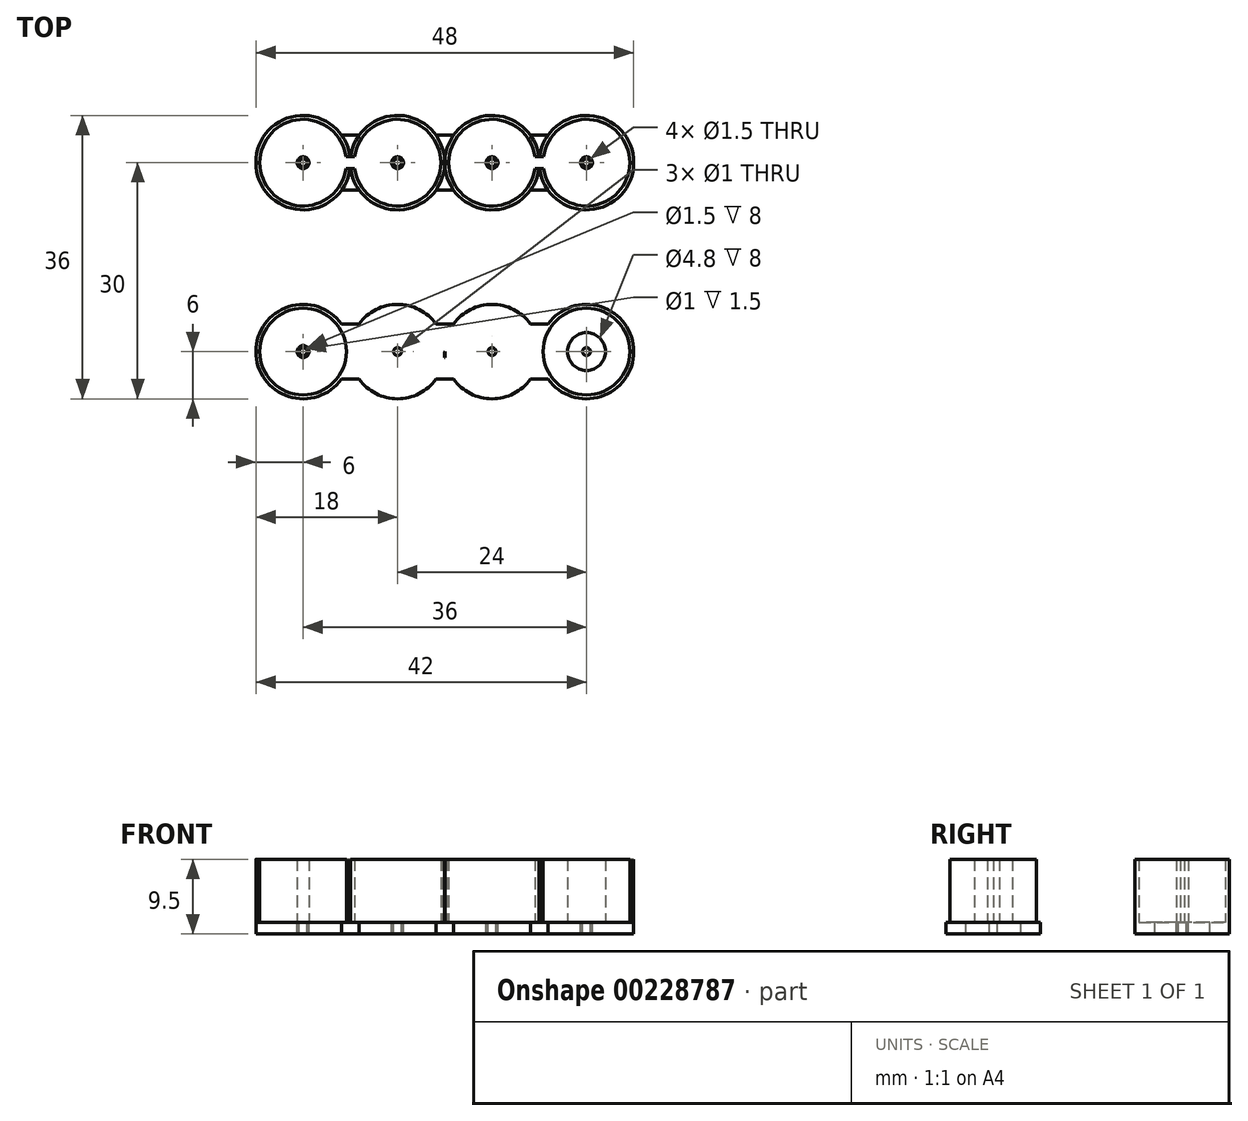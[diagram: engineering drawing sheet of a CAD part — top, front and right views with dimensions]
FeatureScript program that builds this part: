
annotation { "Feature Type Name" : "Feature", "Feature Type Description" : "" }
export const myFeature = defineFeature(function(context is Context, id is Id, definition is map)
    precondition{}
    {
        {
            var Q0;
            Q0=qCreatedBy(makeId("Top.planeOp"),FACE);
            var sketch = newSketch(context, id + "F0", { "sketchPlane" : qUnion([Q0])});
            skCircle(sketch, "E0", {"center": v(-18, 0) * mm, "radius": 6 * mm});
            skCircle(sketch, "E1", {"center": v(-6, 0) * mm, "radius": 6 * mm});
            skCircle(sketch, "E2", {"center": v(6, 0) * mm, "radius": 6 * mm});
            skCircle(sketch, "E3", {"center": v(18, 0) * mm, "radius": 6 * mm});
            skPoint(sketch, "E4", {"position": v(0, 0) * mm});
            skCircle(sketch, "E5", {"center": v(-18, 0) * mm, "radius": 5.5 * mm});
            skCircle(sketch, "E6", {"center": v(-6, 0) * mm, "radius": 5.5 * mm});
            skCircle(sketch, "E7", {"center": v(6, 0) * mm, "radius": 5.5 * mm});
            skCircle(sketch, "E8", {"center": v(18, 0) * mm, "radius": 5.5 * mm});
            skLineSegment(sketch, "E9", {"start": v(0, 0) * mm, "end": v(0, -12) * mm, "construction": true});
            skLineSegment(sketch, "E10", {"start": v(0, -12) * mm, "end": v(-21.8, -12) * mm, "construction": true});
            skCircle(sketch, "E11.MirrorC", {"center": v(-18, -24) * mm, "radius": 6 * mm});
            skCircle(sketch, "E12.MirrorC", {"center": v(-6, -24) * mm, "radius": 6 * mm});
            skCircle(sketch, "E13.MirrorC", {"center": v(6, -24) * mm, "radius": 6 * mm});
            skCircle(sketch, "E14.MirrorC", {"center": v(18, -24) * mm, "radius": 6 * mm});
            skCircle(sketch, "E15.MirrorC", {"center": v(-18, -24) * mm, "radius": 5.5 * mm});
            skCircle(sketch, "E16.MirrorC", {"center": v(6, -24) * mm, "radius": 5.5 * mm});
            skPoint(sketch, "E17.MirrorP", {"position": v(0, -24) * mm});
            skCircle(sketch, "E18.MirrorC", {"center": v(18, -24) * mm, "radius": 5.5 * mm});
            skCircle(sketch, "E19.MirrorC", {"center": v(-6, -24) * mm, "radius": 5.5 * mm});
            skCircle(sketch, "E20", {"center": v(-18, 0) * mm, "radius": 1.9 * mm});
            skCircle(sketch, "E21", {"center": v(-18, 0) * mm, "radius": 2.4 * mm});
            skCircle(sketch, "E22", {"center": v(6, 0) * mm, "radius": 1.9 * mm});
            skCircle(sketch, "E23", {"center": v(6, 0) * mm, "radius": 2.4 * mm});
            skCircle(sketch, "E24", {"center": v(-6, -24) * mm, "radius": 2.4 * mm});
            skCircle(sketch, "E25", {"center": v(-6, -24) * mm, "radius": 1.9 * mm});
            skCircle(sketch, "E26", {"center": v(18, -24) * mm, "radius": 2.4 * mm});
            skCircle(sketch, "E27", {"center": v(18, -24) * mm, "radius": 1.9 * mm});
            skCircle(sketch, "E28", {"center": v(-18, 0) * mm, "radius": 0.75 * mm});
            skCircle(sketch, "E29", {"center": v(-6, 0) * mm, "radius": 0.75 * mm});
            skCircle(sketch, "E30", {"center": v(6, 0) * mm, "radius": 0.75 * mm});
            skCircle(sketch, "E31", {"center": v(18, 0) * mm, "radius": 0.75 * mm});
            skCircle(sketch, "E32", {"center": v(18, -24) * mm, "radius": 0.75 * mm});
            skCircle(sketch, "E33", {"center": v(6, -24) * mm, "radius": 0.75 * mm});
            skCircle(sketch, "E34", {"center": v(-6, -24) * mm, "radius": 0.75 * mm});
            skCircle(sketch, "E35", {"center": v(-18, -24) * mm, "radius": 0.75 * mm});
            skLineSegment(sketch, "E36", {"start": v(-18, 0.75) * mm, "end": v(-6, 0.75) * mm});
            skLineSegment(sketch, "E37.MirrorCS", {"start": v(-18, -0.75) * mm, "end": v(-6, -0.75) * mm});
            skLineSegment(sketch, "E38.MirrorCS", {"start": v(18, 0.75) * mm, "end": v(6, 0.75) * mm});
            skLineSegment(sketch, "E39.MirrorCS", {"start": v(18, -0.75) * mm, "end": v(6, -0.75) * mm});
            skLineSegment(sketch, "E40", {"start": v(-6, -23.25) * mm, "end": v(6, -23.25) * mm});
            skLineSegment(sketch, "E41", {"start": v(-6, -24.75) * mm, "end": v(6, -24.75) * mm});
            skCircle(sketch, "E42", {"center": v(-18, -24) * mm, "radius": 0.5 * mm});
            skCircle(sketch, "E43", {"center": v(18, -24) * mm, "radius": 0.5 * mm});
            skCircle(sketch, "E44", {"center": v(0, 0) * mm, "radius": 0.25 * mm});
            skCircle(sketch, "E45", {"center": v(-12, -24) * mm, "radius": 0.25 * mm});
            skCircle(sketch, "E46", {"center": v(12, -24) * mm, "radius": 0.25 * mm});
            skCircle(sketch, "E47", {"center": v(6, -24) * mm, "radius": 0.5 * mm});
            skCircle(sketch, "E48", {"center": v(-6, -24) * mm, "radius": 0.5 * mm});
            skCircle(sketch, "E49.MirrorC", {"center": v(6, 0) * mm, "radius": 0.5 * mm});
            skCircle(sketch, "E50.MirrorC", {"center": v(-6, 0) * mm, "radius": 0.5 * mm});
            skCircle(sketch, "E51.MirrorC", {"center": v(-18, 0) * mm, "radius": 0.5 * mm});
            skCircle(sketch, "E52.MirrorC", {"center": v(18, 0) * mm, "radius": 0.5 * mm});
            skSolve(sketch);
        }
        {
            var Q0;
            Q0=qCreatedBy(makeId("Top.planeOp"),FACE);
            var sketch = newSketch(context, id + "F1", { "sketchPlane" : qUnion([Q0])});
            skArc(sketch, "E53.0", {"start": v(-13.13, 3.5) * mm, "mid": v(-24, 0) * mm, "end": v(-13.13, -3.5) * mm});
            skArc(sketch, "E53.1", {"start": v(-10.87, -3.5) * mm, "mid": v(-6, -6) * mm, "end": v(-1.13, -3.5) * mm});
            skArc(sketch, "E53.2", {"start": v(1.13, -3.5) * mm, "mid": v(6, -6) * mm, "end": v(10.87, -3.5) * mm});
            skArc(sketch, "E53.3", {"start": v(13.13, -3.5) * mm, "mid": v(24, 0) * mm, "end": v(13.13, 3.5) * mm});
            skLineSegment(sketch, "E54.bottom", {"start": v(-13.13, 3.5) * mm, "end": v(-10.87, 3.5) * mm});
            skLineSegment(sketch, "E54.top", {"start": v(-13.13, -3.5) * mm, "end": v(-10.87, -3.5) * mm});
            skPoint(sketch, "E54.middle", {"position": v(0, 0) * mm});
            skPoint(sketch, "E54.left.start.orphan", {"position": v(-15, 3.5) * mm});
            skPoint(sketch, "E55.orphan", {"position": v(-15, -3.5) * mm});
            skLineSegment(sketch, "E56.trimOffspring", {"start": v(-1.13, -3.5) * mm, "end": v(1.13, -3.5) * mm});
            skLineSegment(sketch, "E57.trimOffspring", {"start": v(-1.13, 3.5) * mm, "end": v(1.13, 3.5) * mm});
            skLineSegment(sketch, "E58.trimOffspring", {"start": v(10.87, 3.5) * mm, "end": v(13.13, 3.5) * mm});
            skLineSegment(sketch, "E59.trimOffspring", {"start": v(10.87, -3.5) * mm, "end": v(13.13, -3.5) * mm});
            skPoint(sketch, "E60.orphan", {"position": v(15, 3.5) * mm});
            skPoint(sketch, "E61.orphan", {"position": v(15, -3.5) * mm});
            skLineSegment(sketch, "E62.MirrorCS", {"start": v(-13.13, -20.5) * mm, "end": v(-10.87, -20.5) * mm});
            skLineSegment(sketch, "E63.MirrorCS", {"start": v(-13.13, -27.5) * mm, "end": v(-10.87, -27.5) * mm});
            skLineSegment(sketch, "E64.MirrorCS", {"start": v(-1.13, -27.5) * mm, "end": v(1.13, -27.5) * mm});
            skLineSegment(sketch, "E65.MirrorCS", {"start": v(-1.13, -20.5) * mm, "end": v(1.13, -20.5) * mm});
            skLineSegment(sketch, "E66.MirrorCS", {"start": v(10.87, -20.5) * mm, "end": v(13.13, -20.5) * mm});
            skLineSegment(sketch, "E67.MirrorCS", {"start": v(10.87, -27.5) * mm, "end": v(13.13, -27.5) * mm});
            skArc(sketch, "E68.trimOffspring", {"start": v(-1.13, 3.5) * mm, "mid": v(-6, 6) * mm, "end": v(-10.87, 3.5) * mm});
            skArc(sketch, "E69.trimOffspring", {"start": v(10.87, 3.5) * mm, "mid": v(6, 6) * mm, "end": v(1.13, 3.5) * mm});
            skArc(sketch, "E70.MirrorCS", {"start": v(-13.13, -27.5) * mm, "mid": v(-24, -24) * mm, "end": v(-13.13, -20.5) * mm});
            skArc(sketch, "E71.MirrorCS", {"start": v(-10.87, -20.5) * mm, "mid": v(-6, -18) * mm, "end": v(-1.13, -20.5) * mm});
            skArc(sketch, "E72.MirrorCS", {"start": v(1.13, -20.5) * mm, "mid": v(6, -18) * mm, "end": v(10.87, -20.5) * mm});
            skArc(sketch, "E73.MirrorCS", {"start": v(13.13, -20.5) * mm, "mid": v(24, -24) * mm, "end": v(13.13, -27.5) * mm});
            skArc(sketch, "E74.MirrorCS", {"start": v(10.87, -27.5) * mm, "mid": v(6, -30) * mm, "end": v(1.13, -27.5) * mm});
            skArc(sketch, "E75.MirrorCS", {"start": v(-1.13, -27.5) * mm, "mid": v(-6, -30) * mm, "end": v(-10.87, -27.5) * mm});
            skSolve(sketch);
        }
        {
            var Q0;
            Q0=makeQuery(id+"F1.imprint","IMPRINT",FACE,{"disambiguationData":[TD([[makeQuery(id+"F1.imprint","IMPRINT",EDGE,{"derivedFrom":sQuery(id+"F1.wireOp",EDGE,"E53.0")}),1.0]])]});
            extrude(context, id + "F2", {"entities" : qUnion([Q0]), "oppositeDirection" : true, "depth" : 1.5 * mm});
        }
        {
            var Q0;
            {var subQ0=sQuery(id+"F0.wireOp",EDGE,"E36");var subQ1=sQuery(id+"F0.wireOp",EDGE,"E0");var subQ2=makeQuery(id+"F0.imprint","INTERSECT",VERTEX,{"derivedFrom":[subQ1,subQ0]});Q0=makeQuery(id+"F0.imprint","IMPRINT",FACE,{"disambiguationData":[TD([[makeQuery(id+"F0.imprint","IMPRINT",EDGE,{"disambiguationData":[TD([[subQ2,-1.0]])],"derivedFrom":subQ1}),1.0]])]});}
            var Q1;
            {var subQ1=sQuery(id+"F0.wireOp",EDGE,"E1");var subQ7=sQuery(id+"F0.wireOp",EDGE,"E44");var subQ8=makeQuery(id+"F0.imprint","INTERSECT",VERTEX,{"disambiguationData":[OD(0.0)],"derivedFrom":[subQ1,subQ7]});Q1=makeQuery(id+"F0.imprint","IMPRINT",FACE,{"disambiguationData":[TD([[makeQuery(id+"F0.imprint","IMPRINT",EDGE,{"disambiguationData":[TD([[subQ8,-1.0]])],"derivedFrom":subQ1}),1.0]])]});}
            var Q2;
            {var subQ0=sQuery(id+"F0.wireOp",EDGE,"E38.MirrorCS");var subQ1=sQuery(id+"F0.wireOp",EDGE,"E2");var subQ2=makeQuery(id+"F0.imprint","INTERSECT",VERTEX,{"derivedFrom":[subQ1,subQ0]});Q2=makeQuery(id+"F0.imprint","IMPRINT",FACE,{"disambiguationData":[TD([[makeQuery(id+"F0.imprint","IMPRINT",EDGE,{"disambiguationData":[TD([[subQ2,-1.0]])],"derivedFrom":subQ1}),1.0]])]});}
            var Q3;
            {var subQ0=sQuery(id+"F0.wireOp",EDGE,"E38.MirrorCS");var subQ1=sQuery(id+"F0.wireOp",EDGE,"E3");var subQ2=makeQuery(id+"F0.imprint","INTERSECT",VERTEX,{"derivedFrom":[subQ1,subQ0]});Q3=makeQuery(id+"F0.imprint","IMPRINT",FACE,{"disambiguationData":[TD([[makeQuery(id+"F0.imprint","IMPRINT",EDGE,{"disambiguationData":[TD([[subQ2,1.0]])],"derivedFrom":subQ1}),1.0]])]});}
            extrude(context, id + "F3", {"entities" : qUnion([Q0, Q1, Q2, Q3]), "operationType" : NewBodyOperationType.ADD, "depth" : 8 * mm});
        }
        {
            var Q0;
            Q0=makeQuery(id+"F1.imprint","IMPRINT",FACE,{"disambiguationData":[TD([[makeQuery(id+"F1.imprint","IMPRINT",EDGE,{"derivedFrom":sQuery(id+"F1.wireOp",EDGE,"E62.MirrorCS")}),-1.0]])]});
            extrude(context, id + "F4", {"entities" : qUnion([Q0]), "oppositeDirection" : true, "depth" : 1.5 * mm});
        }
        {
            var Q0;
            Q0=makeQuery(id+"F0.imprint","IMPRINT",FACE,{"disambiguationData":[TD([[makeQuery(id+"F0.imprint","IMPRINT",EDGE,{"derivedFrom":sQuery(id+"F0.wireOp",EDGE,"E15.MirrorC")}),1.0]])]});
            var Q1;
            {var subQ1=sQuery(id+"F0.wireOp",EDGE,"E12.MirrorC");var subQ7=sQuery(id+"F0.wireOp",EDGE,"E41");var subQ8=makeQuery(id+"F0.imprint","INTERSECT",VERTEX,{"derivedFrom":[subQ1,subQ7]});Q1=makeQuery(id+"F0.imprint","IMPRINT",FACE,{"disambiguationData":[TD([[makeQuery(id+"F0.imprint","IMPRINT",EDGE,{"disambiguationData":[TD([[subQ8,-1.0]])],"derivedFrom":subQ1}),-1.0]])]});}
            var Q2;
            {var subQ1=sQuery(id+"F0.wireOp",EDGE,"E13.MirrorC");var subQ8=sQuery(id+"F0.wireOp",EDGE,"E46");var subQ10=makeQuery(id+"F0.imprint","INTERSECT",VERTEX,{"disambiguationData":[OD(0.0)],"derivedFrom":[subQ1,subQ8]});Q2=makeQuery(id+"F0.imprint","IMPRINT",FACE,{"disambiguationData":[TD([[makeQuery(id+"F0.imprint","IMPRINT",EDGE,{"disambiguationData":[TD([[subQ10,-1.0]])],"derivedFrom":subQ1}),-1.0]])]});}
            var Q3;
            Q3=makeQuery(id+"F0.imprint","IMPRINT",FACE,{"disambiguationData":[TD([[makeQuery(id+"F0.imprint","IMPRINT",EDGE,{"derivedFrom":sQuery(id+"F0.wireOp",EDGE,"E18.MirrorC")}),1.0]])]});
            extrude(context, id + "F5", {"entities" : qUnion([Q0, Q1, Q2, Q3]), "operationType" : NewBodyOperationType.ADD, "depth" : 8 * mm});
        }
        {
            var Q0;
            Q0=makeQuery(id+"F0.imprint","IMPRINT",FACE,{"disambiguationData":[TD([[makeQuery(id+"F0.imprint","IMPRINT",EDGE,{"derivedFrom":sQuery(id+"F0.wireOp",EDGE,"E43")}),1.0]])]});
            var Q1;
            Q1=makeQuery(id+"F0.imprint","IMPRINT",FACE,{"disambiguationData":[TD([[makeQuery(id+"F0.imprint","IMPRINT",EDGE,{"derivedFrom":sQuery(id+"F0.wireOp",EDGE,"E42")}),1.0]])]});
            var Q2;
            Q2=makeQuery(id+"F0.imprint","IMPRINT",FACE,{"disambiguationData":[TD([[makeQuery(id+"F0.imprint","IMPRINT",EDGE,{"derivedFrom":sQuery(id+"F0.wireOp",EDGE,"E47")}),1.0]])]});
            var Q3;
            Q3=makeQuery(id+"F0.imprint","IMPRINT",FACE,{"disambiguationData":[TD([[makeQuery(id+"F0.imprint","IMPRINT",EDGE,{"derivedFrom":sQuery(id+"F0.wireOp",EDGE,"E48")}),1.0]])]});
            extrude(context, id + "F6", {"entities" : qUnion([Q0, Q1, Q2, Q3]), "operationType" : NewBodyOperationType.REMOVE, "oppositeDirection" : true, "depth" : 25 * mm});
        }
        {
            var Q0;
            Q0=makeQuery(id+"F0.imprint","IMPRINT",FACE,{"disambiguationData":[TD([[makeQuery(id+"F0.imprint","IMPRINT",EDGE,{"derivedFrom":sQuery(id+"F0.wireOp",EDGE,"E52.MirrorC")}),-1.0]])]});
            var Q1;
            Q1=makeQuery(id+"F0.imprint","IMPRINT",FACE,{"disambiguationData":[TD([[makeQuery(id+"F0.imprint","IMPRINT",EDGE,{"derivedFrom":sQuery(id+"F0.wireOp",EDGE,"E49.MirrorC")}),-1.0]])]});
            var Q2;
            Q2=makeQuery(id+"F0.imprint","IMPRINT",FACE,{"disambiguationData":[TD([[makeQuery(id+"F0.imprint","IMPRINT",EDGE,{"derivedFrom":sQuery(id+"F0.wireOp",EDGE,"E50.MirrorC")}),-1.0]])]});
            var Q3;
            Q3=makeQuery(id+"F0.imprint","IMPRINT",FACE,{"disambiguationData":[TD([[makeQuery(id+"F0.imprint","IMPRINT",EDGE,{"derivedFrom":sQuery(id+"F0.wireOp",EDGE,"E51.MirrorC")}),-1.0]])]});
            extrude(context, id + "F7", {"entities" : qUnion([Q0, Q1, Q2, Q3]), "operationType" : NewBodyOperationType.REMOVE, "oppositeDirection" : true, "depth" : 25 * mm});
        }
    });
